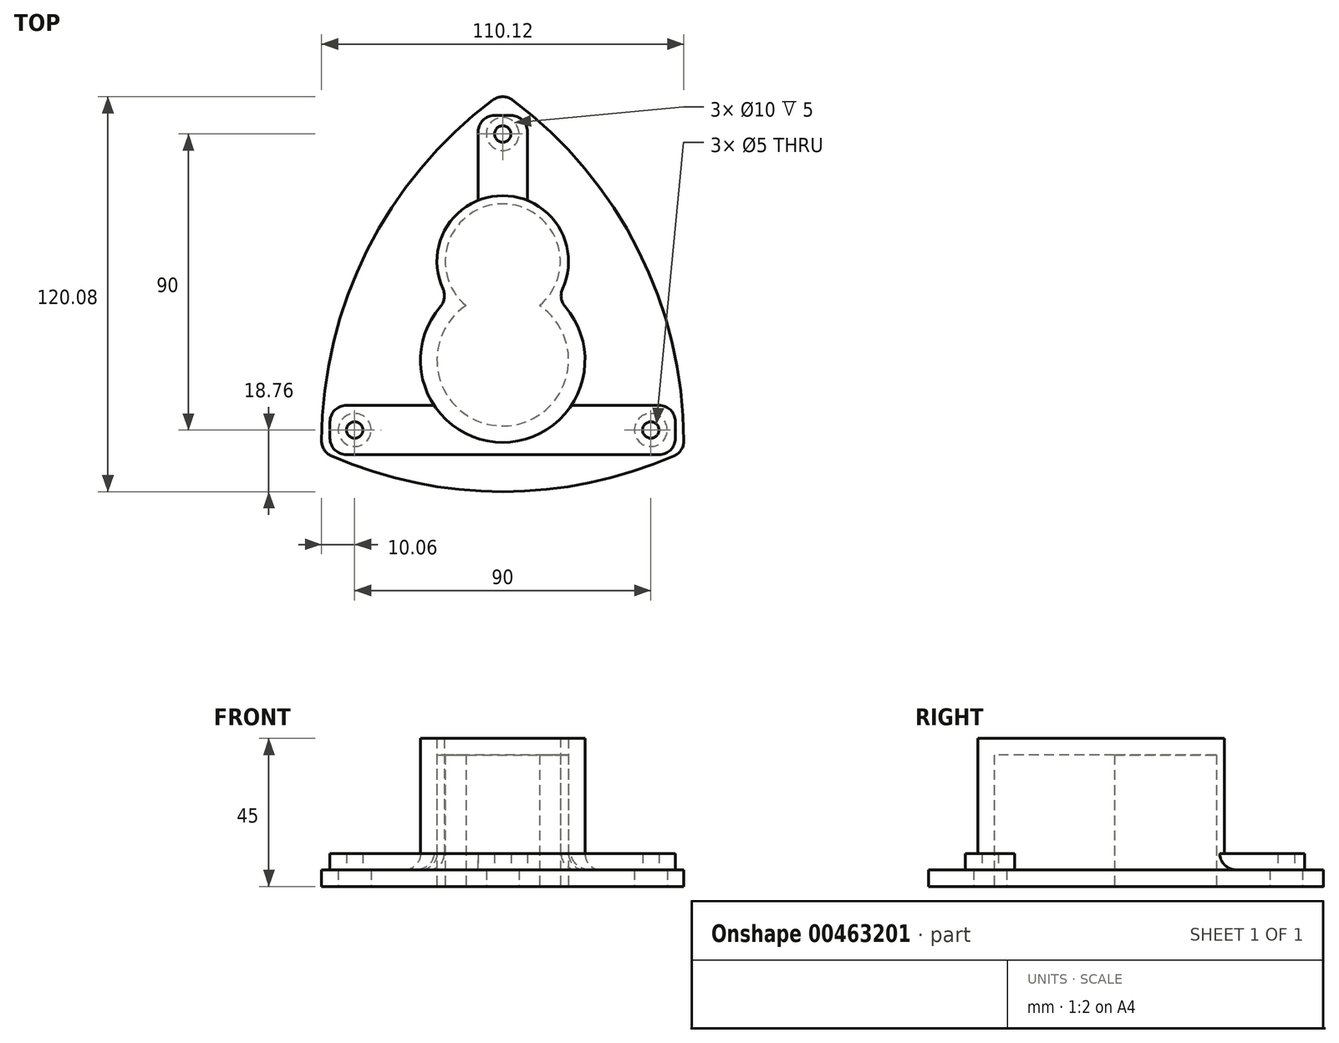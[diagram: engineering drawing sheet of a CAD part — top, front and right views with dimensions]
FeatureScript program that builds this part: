
annotation { "Feature Type Name" : "Feature", "Feature Type Description" : "" }
export const myFeature = defineFeature(function(context is Context, id is Id, definition is map)
    precondition{}
    {
        {
            var Q0;
            Q0=qCreatedBy(makeId("Top.planeOp"),FACE);
            var sketch = newSketch(context, id + "F0", { "sketchPlane" : qUnion([Q0])});
            skPoint(sketch, "E0.middle", {"position": v(0, 0) * mm});
            skCircle(sketch, "E1", {"center": v(-45, -45) * mm, "radius": 2.5 * mm});
            skCircle(sketch, "E2", {"center": v(45, -45) * mm, "radius": 2.5 * mm});
            skCircle(sketch, "E3", {"center": v(0, 45) * mm, "radius": 2.5 * mm});
            skCircle(sketch, "E4", {"center": v(0, 45) * mm, "radius": 5 * mm});
            skCircle(sketch, "E5", {"center": v(45, -45) * mm, "radius": 5 * mm});
            skCircle(sketch, "E6", {"center": v(-45, -45) * mm, "radius": 5 * mm});
            skSolve(sketch);
        }
        {
            var Q0;
            Q0=qCreatedBy(makeId("Top.planeOp"),FACE);
            var sketch = newSketch(context, id + "F1", { "sketchPlane" : qUnion([Q0])});
            skPoint(sketch, "E7.0", {"position": v(0, 45) * mm});
            skPoint(sketch, "E7.1", {"position": v(-45, -45) * mm});
            skPoint(sketch, "E7.2", {"position": v(45, -45) * mm});
            skArc(sketch, "E8", {"start": v(0, 45) * mm, "mid": v(-32.39, 4.94) * mm, "end": v(-45, -45) * mm});
            skArc(sketch, "E9", {"start": v(45, -45) * mm, "mid": v(32.39, 4.94) * mm, "end": v(0, 45) * mm});
            skArc(sketch, "E10", {"start": v(-45, -45) * mm, "mid": v(0, -53.76) * mm, "end": v(45, -45) * mm});
            skArc(sketch, "E11.0", {"start": v(0, 57.5) * mm, "mid": v(-41.12, 9.85) * mm, "end": v(-55.03, -51.54) * mm});
            skArc(sketch, "E11.1", {"start": v(55.03, -51.54) * mm, "mid": v(41.12, 9.85) * mm, "end": v(0, 57.5) * mm});
            skArc(sketch, "E11.2", {"start": v(-55.03, -51.54) * mm, "mid": v(0, -63.76) * mm, "end": v(55.03, -51.54) * mm});
            skSolve(sketch);
        }
        {
            var Q0;
            Q0=qCreatedBy(makeId("Top.planeOp"),FACE);
            var sketch = newSketch(context, id + "F2", { "sketchPlane" : qUnion([Q0])});
            skPoint(sketch, "E12.0", {"position": v(0, 57.5) * mm});
            skPoint(sketch, "E12.1", {"position": v(0, 0) * mm});
            skPoint(sketch, "E13.0", {"position": v(0, -63.76) * mm});
            skLineSegment(sketch, "E14", {"start": v(0, 57.5) * mm, "end": v(0, -63.76) * mm, "construction": true});
            skCircle(sketch, "E15", {"center": v(0, -23.76) * mm, "radius": 20 * mm});
            skCircle(sketch, "E16", {"center": v(0, -23.76) * mm, "radius": 25 * mm});
            skSolve(sketch);
        }
        {
            var Q0;
            Q0=qCreatedBy(makeId("Top.planeOp"),FACE);
            var sketch = newSketch(context, id + "F3", { "sketchPlane" : qUnion([Q0])});
            skPoint(sketch, "E17", {"position": v(0, 6.24) * mm});
            skCircle(sketch, "E18", {"center": v(0, 6.24) * mm, "radius": 20 * mm});
            skSolve(sketch);
        }
        {
            var Q0;
            Q0=qCreatedBy(makeId("Top.planeOp"),FACE);
            var sketch = newSketch(context, id + "F4", { "sketchPlane" : qUnion([Q0])});
            skPoint(sketch, "E19.0", {"position": v(-45, -45) * mm});
            skPoint(sketch, "E19.1", {"position": v(45, -45) * mm});
            skPoint(sketch, "E19.2", {"position": v(0, 45) * mm});
            skLineSegment(sketch, "E20", {"start": v(-45, -45) * mm, "end": v(45, -45) * mm});
            skLineSegment(sketch, "E21", {"start": v(0, 45) * mm, "end": v(0, -45) * mm});
            skLineSegment(sketch, "E22.bottom", {"start": v(52.5, -52.5) * mm, "end": v(-52.5, -52.5) * mm});
            skLineSegment(sketch, "E22.top", {"start": v(52.5, -37.5) * mm, "end": v(-52.5, -37.5) * mm});
            skLineSegment(sketch, "E22.left", {"start": v(52.5, -52.5) * mm, "end": v(52.5, -37.5) * mm});
            skLineSegment(sketch, "E22.right", {"start": v(-52.5, -52.5) * mm, "end": v(-52.5, -37.5) * mm});
            skPoint(sketch, "E22.middle", {"position": v(0, -45) * mm});
            skPoint(sketch, "E23.1", {"position": v(0, 0) * mm});
            skLineSegment(sketch, "E24.bottom", {"start": v(7.5, 10.63) * mm, "end": v(-7.5, 10.63) * mm});
            skLineSegment(sketch, "E24.top", {"start": v(7.5, 50.63) * mm, "end": v(-7.5, 50.63) * mm});
            skLineSegment(sketch, "E24.left", {"start": v(7.5, 10.63) * mm, "end": v(7.5, 50.63) * mm});
            skLineSegment(sketch, "E24.right", {"start": v(-7.5, 10.63) * mm, "end": v(-7.5, 50.63) * mm});
            skPoint(sketch, "E24.middle", {"position": v(0, 30.63) * mm});
            skSolve(sketch);
        }
        {
            var Q0;
            Q0=makeQuery(id+"F1.imprint","IMPRINT",FACE,{"disambiguationData":[TD([[makeQuery(id+"F1.imprint","IMPRINT",EDGE,{"derivedFrom":sQuery(id+"F1.wireOp",EDGE,"E8")}),1.0]])]});
            var Q1;
            Q1=makeQuery(id+"F1.imprint","IMPRINT",FACE,{"disambiguationData":[TD([[makeQuery(id+"F1.imprint","IMPRINT",EDGE,{"derivedFrom":sQuery(id+"F1.wireOp",EDGE,"E8")}),-1.0]])]});
            extrude(context, id + "F5", {"entities" : qUnion([Q0, Q1]), "depth" : 5 * mm});
        }
        {
            var Q0;
            Q0=makeQuery(id+"F3.imprint","IMPRINT",FACE,{"disambiguationData":[TD([[makeQuery(id+"F3.imprint","IMPRINT",EDGE,{"derivedFrom":sQuery(id+"F3.wireOp",EDGE,"E18")}),1.0]])]});
            var Q1;
            Q1=makeQuery(id+"F2.imprint","IMPRINT",FACE,{"disambiguationData":[TD([[makeQuery(id+"F2.imprint","IMPRINT",EDGE,{"derivedFrom":sQuery(id+"F2.wireOp",EDGE,"E15")}),1.0]])]});
            var Q2;
            Q2=makeQuery(id+"F2.imprint","IMPRINT",FACE,{"disambiguationData":[TD([[makeQuery(id+"F2.imprint","IMPRINT",EDGE,{"derivedFrom":sQuery(id+"F2.wireOp",EDGE,"E15")}),-1.0]])]});
            extrude(context, id + "F6", {"entities" : qUnion([Q0, Q1, Q2]), "operationType" : NewBodyOperationType.ADD, "depth" : 50 * mm});
        }
        {
            var Q0;
            Q0=makeQuery(id+"F4.imprint","IMPRINT",FACE,{"disambiguationData":[TD([[makeQuery(id+"F4.imprint","IMPRINT",EDGE,{"derivedFrom":sQuery(id+"F4.wireOp",EDGE,"E22.bottom")}),-1.0]])]});
            var Q1;
            Q1=makeQuery(id+"F4.imprint","IMPRINT",FACE,{"disambiguationData":[TD([[makeQuery(id+"F4.imprint","IMPRINT",EDGE,{"derivedFrom":sQuery(id+"F4.wireOp",EDGE,"E24.top")}),1.0]])]});
            extrude(context, id + "F7", {"entities" : qUnion([Q0, Q1]), "operationType" : NewBodyOperationType.ADD, "depth" : 10 * mm});
        }
        {
            var Q0;
            Q0=makeQuery(id+"F0.imprint","IMPRINT",FACE,{"disambiguationData":[TD([[makeQuery(id+"F0.imprint","IMPRINT",EDGE,{"derivedFrom":sQuery(id+"F0.wireOp",EDGE,"E1")}),-1.0]])]});
            var Q1;
            Q1=makeQuery(id+"F0.imprint","IMPRINT",FACE,{"disambiguationData":[TD([[makeQuery(id+"F0.imprint","IMPRINT",EDGE,{"derivedFrom":sQuery(id+"F0.wireOp",EDGE,"E3")}),-1.0]])]});
            var Q2;
            Q2=makeQuery(id+"F0.imprint","IMPRINT",FACE,{"disambiguationData":[TD([[makeQuery(id+"F0.imprint","IMPRINT",EDGE,{"derivedFrom":sQuery(id+"F0.wireOp",EDGE,"E2")}),-1.0]])]});
            extrude(context, id + "F8", {"entities" : qUnion([Q0, Q1, Q2]), "operationType" : NewBodyOperationType.REMOVE, "depth" : 5 * mm});
        }
        {
            var Q0;
            Q0=makeQuery(id+"F0.imprint","IMPRINT",FACE,{"disambiguationData":[TD([[makeQuery(id+"F0.imprint","IMPRINT",EDGE,{"derivedFrom":sQuery(id+"F0.wireOp",EDGE,"E1")}),1.0]])]});
            var Q1;
            Q1=makeQuery(id+"F0.imprint","IMPRINT",FACE,{"disambiguationData":[TD([[makeQuery(id+"F0.imprint","IMPRINT",EDGE,{"derivedFrom":sQuery(id+"F0.wireOp",EDGE,"E3")}),1.0]])]});
            var Q2;
            Q2=makeQuery(id+"F0.imprint","IMPRINT",FACE,{"disambiguationData":[TD([[makeQuery(id+"F0.imprint","IMPRINT",EDGE,{"derivedFrom":sQuery(id+"F0.wireOp",EDGE,"E2")}),1.0]])]});
            extrude(context, id + "F9", {"entities" : qUnion([Q0, Q1, Q2]), "operationType" : NewBodyOperationType.REMOVE, "depth" : 25 * mm});
        }
        {
            var Q0;
            Q0=makeQuery(id+"F3.imprint","IMPRINT",FACE,{"disambiguationData":[TD([[makeQuery(id+"F3.imprint","IMPRINT",EDGE,{"derivedFrom":sQuery(id+"F3.wireOp",EDGE,"E18")}),1.0]])]});
            var sketch = newSketch(context, id + "F10", { "sketchPlane" : qUnion([Q0])});
            skPoint(sketch, "E25.0", {"position": v(0, 6.24) * mm});
            skCircle(sketch, "E26.0.0", {"center": v(0, 6.24) * mm, "radius": 20 * mm});
            skCircle(sketch, "E27", {"center": v(0, 6.24) * mm, "radius": 17.5 * mm});
            skSolve(sketch);
        }
        {
            var Q0;
            Q0=makeQuery(id+"F10.imprint","IMPRINT",FACE,{"disambiguationData":[TD([[makeQuery(id+"F10.imprint","IMPRINT",EDGE,{"derivedFrom":sQuery(id+"F10.wireOp",EDGE,"E27")}),1.0]])]});
            var Q1;
            Q1=makeQuery(id+"F2.imprint","IMPRINT",FACE,{"disambiguationData":[TD([[makeQuery(id+"F2.imprint","IMPRINT",EDGE,{"derivedFrom":sQuery(id+"F2.wireOp",EDGE,"E15")}),1.0]])]});
            extrude(context, id + "F11", {"entities" : qUnion([Q0, Q1]), "operationType" : NewBodyOperationType.REMOVE, "depth" : 40 * mm});
        }
        {
            var Q0;
            Q0=makeQuery(id+"F6.boolean.opBoolean","MERGE",FACE,{"derivedFrom":[makeQuery(id+"F6.opExtrude","CAP_FACE",FACE,{"disambiguationData":[OSD([sQuery(id+"F2.wireOp",EDGE,"E16")])],"isStart":false}),makeQuery(id+"F6.opExtrude","CAP_FACE",FACE,{"disambiguationData":[OSD([sQuery(id+"F3.wireOp",EDGE,"E18")])],"isStart":false})]});
            extrude(context, id + "F12", {"entities" : qUnion([Q0]), "operationType" : NewBodyOperationType.REMOVE, "oppositeDirection" : true, "depth" : 5 * mm});
        }
        {
            var Q0;
            Q0=makeQuery(id+"F7.opExtrude","SWEPT_EDGE",EDGE,{"disambiguationData":[OSD([sQuery(id+"F4.wireOp",EDGE,"E22.bottom"),sQuery(id+"F4.wireOp",EDGE,"E22.left")])]});
            var Q1;
            Q1=makeQuery(id+"F7.opExtrude","SWEPT_EDGE",EDGE,{"disambiguationData":[OSD([sQuery(id+"F4.wireOp",EDGE,"E22.top"),sQuery(id+"F4.wireOp",EDGE,"E22.left")])]});
            var Q2;
            Q2=makeQuery(id+"F5.opExtrude","SWEPT_EDGE",EDGE,{"disambiguationData":[OSD([sQuery(id+"F1.wireOp",EDGE,"E11.1"),sQuery(id+"F1.wireOp",EDGE,"E11.2")])]});
            var Q3;
            Q3=makeQuery(id+"F5.opExtrude","SWEPT_EDGE",EDGE,{"disambiguationData":[OSD([sQuery(id+"F1.wireOp",EDGE,"E11.0"),sQuery(id+"F1.wireOp",EDGE,"E11.2")])]});
            var Q4;
            Q4=makeQuery(id+"F7.opExtrude","SWEPT_EDGE",EDGE,{"disambiguationData":[OSD([sQuery(id+"F4.wireOp",EDGE,"E22.bottom"),sQuery(id+"F4.wireOp",EDGE,"E22.right")])]});
            var Q5;
            Q5=makeQuery(id+"F7.opExtrude","SWEPT_EDGE",EDGE,{"disambiguationData":[OSD([sQuery(id+"F4.wireOp",EDGE,"E22.top"),sQuery(id+"F4.wireOp",EDGE,"E22.right")])]});
            var Q6;
            Q6=makeQuery(id+"F7.opExtrude","SWEPT_EDGE",EDGE,{"disambiguationData":[OSD([sQuery(id+"F4.wireOp",EDGE,"E24.top"),sQuery(id+"F4.wireOp",EDGE,"E24.right")])]});
            var Q7;
            Q7=makeQuery(id+"F5.opExtrude","SWEPT_EDGE",EDGE,{"disambiguationData":[OSD([sQuery(id+"F1.wireOp",EDGE,"E11.0"),sQuery(id+"F1.wireOp",EDGE,"E11.1")])]});
            var Q8;
            Q8=makeQuery(id+"F7.opExtrude","SWEPT_EDGE",EDGE,{"disambiguationData":[OSD([sQuery(id+"F4.wireOp",EDGE,"E24.top"),sQuery(id+"F4.wireOp",EDGE,"E24.left")])]});
            fillet(context, id + "F13", {"entities" : qUnion([Q0, Q1, Q2, Q3, Q4, Q5, Q6, Q7, Q8]), "radius" : 5 * mm, "tangentPropagation" : true, "allowEdgeOverflow" : false});
        }
        {
            var Q0;
            {var subQ0=makeQuery(id+"F5.opExtrude","CAP_FACE",FACE,{"disambiguationData":[OSD([sQuery(id+"F1.wireOp",EDGE,"E11.0"),sQuery(id+"F1.wireOp",EDGE,"E11.1"),sQuery(id+"F1.wireOp",EDGE,"E11.2")])],"isStart":false});var subQ1=makeQuery(id+"F6.opExtrude","SWEPT_FACE",FACE,{"disambiguationData":[OSD([sQuery(id+"F3.wireOp",EDGE,"E18")])]});Q0=makeQuery(id+"F7.boolean.opBoolean","SPLIT",EDGE,{"disambiguationData":[TD([makeQuery(id+"F7.opExtrude","SWEPT_FACE",FACE,{"disambiguationData":[OSD([sQuery(id+"F4.wireOp",EDGE,"E24.left")])]})])],"derivedFrom":makeQuery(id+"F6.boolean.opBoolean","INTERSECT",EDGE,{"derivedFrom":[subQ0,subQ1]})});}
            var Q1;
            Q1=makeQuery(id+"F7.boolean.opBoolean","SPLIT",EDGE,{"disambiguationData":[OD(1.0)],"derivedFrom":makeQuery(id+"F6.boolean.opBoolean","INTERSECT",EDGE,{"derivedFrom":[makeQuery(id+"F5.opExtrude","CAP_FACE",FACE,{"disambiguationData":[OSD([sQuery(id+"F1.wireOp",EDGE,"E11.0"),sQuery(id+"F1.wireOp",EDGE,"E11.1"),sQuery(id+"F1.wireOp",EDGE,"E11.2")])],"isStart":false}),makeQuery(id+"F6.opExtrude","SWEPT_FACE",FACE,{"disambiguationData":[OSD([sQuery(id+"F2.wireOp",EDGE,"E16")])]})]})});
            var Q2;
            Q2=makeQuery(id+"F7.boolean.opBoolean","SPLIT",EDGE,{"disambiguationData":[OD(0.0)],"derivedFrom":makeQuery(id+"F6.boolean.opBoolean","INTERSECT",EDGE,{"derivedFrom":[makeQuery(id+"F5.opExtrude","CAP_FACE",FACE,{"disambiguationData":[OSD([sQuery(id+"F1.wireOp",EDGE,"E11.0"),sQuery(id+"F1.wireOp",EDGE,"E11.1"),sQuery(id+"F1.wireOp",EDGE,"E11.2")])],"isStart":false}),makeQuery(id+"F6.opExtrude","SWEPT_FACE",FACE,{"disambiguationData":[OSD([sQuery(id+"F2.wireOp",EDGE,"E16")])]})]})});
            var Q3;
            {var subQ0=makeQuery(id+"F5.opExtrude","CAP_FACE",FACE,{"disambiguationData":[OSD([sQuery(id+"F1.wireOp",EDGE,"E11.0"),sQuery(id+"F1.wireOp",EDGE,"E11.1"),sQuery(id+"F1.wireOp",EDGE,"E11.2")])],"isStart":false});var subQ1=makeQuery(id+"F6.opExtrude","SWEPT_FACE",FACE,{"disambiguationData":[OSD([sQuery(id+"F3.wireOp",EDGE,"E18")])]});Q3=makeQuery(id+"F7.boolean.opBoolean","SPLIT",EDGE,{"disambiguationData":[TD([makeQuery(id+"F7.opExtrude","SWEPT_FACE",FACE,{"disambiguationData":[OSD([sQuery(id+"F4.wireOp",EDGE,"E24.right")])]})])],"derivedFrom":makeQuery(id+"F6.boolean.opBoolean","INTERSECT",EDGE,{"derivedFrom":[subQ0,subQ1]})});}
            var Q4;
            Q4=makeQuery(id+"F6.boolean.opBoolean","INTERSECT",EDGE,{"disambiguationData":[OD(0.0)],"derivedFrom":[makeQuery(id+"F6.opExtrude","SWEPT_FACE",FACE,{"disambiguationData":[OSD([sQuery(id+"F2.wireOp",EDGE,"E16")])]}),makeQuery(id+"F6.opExtrude","SWEPT_FACE",FACE,{"disambiguationData":[OSD([sQuery(id+"F3.wireOp",EDGE,"E18")])]})]});
            var Q5;
            Q5=makeQuery(id+"F6.boolean.opBoolean","INTERSECT",EDGE,{"disambiguationData":[OD(1.0)],"derivedFrom":[makeQuery(id+"F6.opExtrude","SWEPT_FACE",FACE,{"disambiguationData":[OSD([sQuery(id+"F2.wireOp",EDGE,"E16")])]}),makeQuery(id+"F6.opExtrude","SWEPT_FACE",FACE,{"disambiguationData":[OSD([sQuery(id+"F3.wireOp",EDGE,"E18")])]})]});
            var Q6;
            Q6=makeQuery(id+"F12.boolean.opBoolean","COPY",EDGE,{"derivedFrom":makeQuery(id+"F12.opExtrude","CAP_EDGE",EDGE,{"disambiguationData":[OSD([sQuery(id+"F3.wireOp",EDGE,"E18")])],"isStart":false})});
            fillet(context, id + "F14", {"entities" : qUnion([Q0, Q1, Q2, Q3, Q4, Q5, Q6]), "radius" : 5 * mm, "tangentPropagation" : true, "allowEdgeOverflow" : false});
        }
    });
